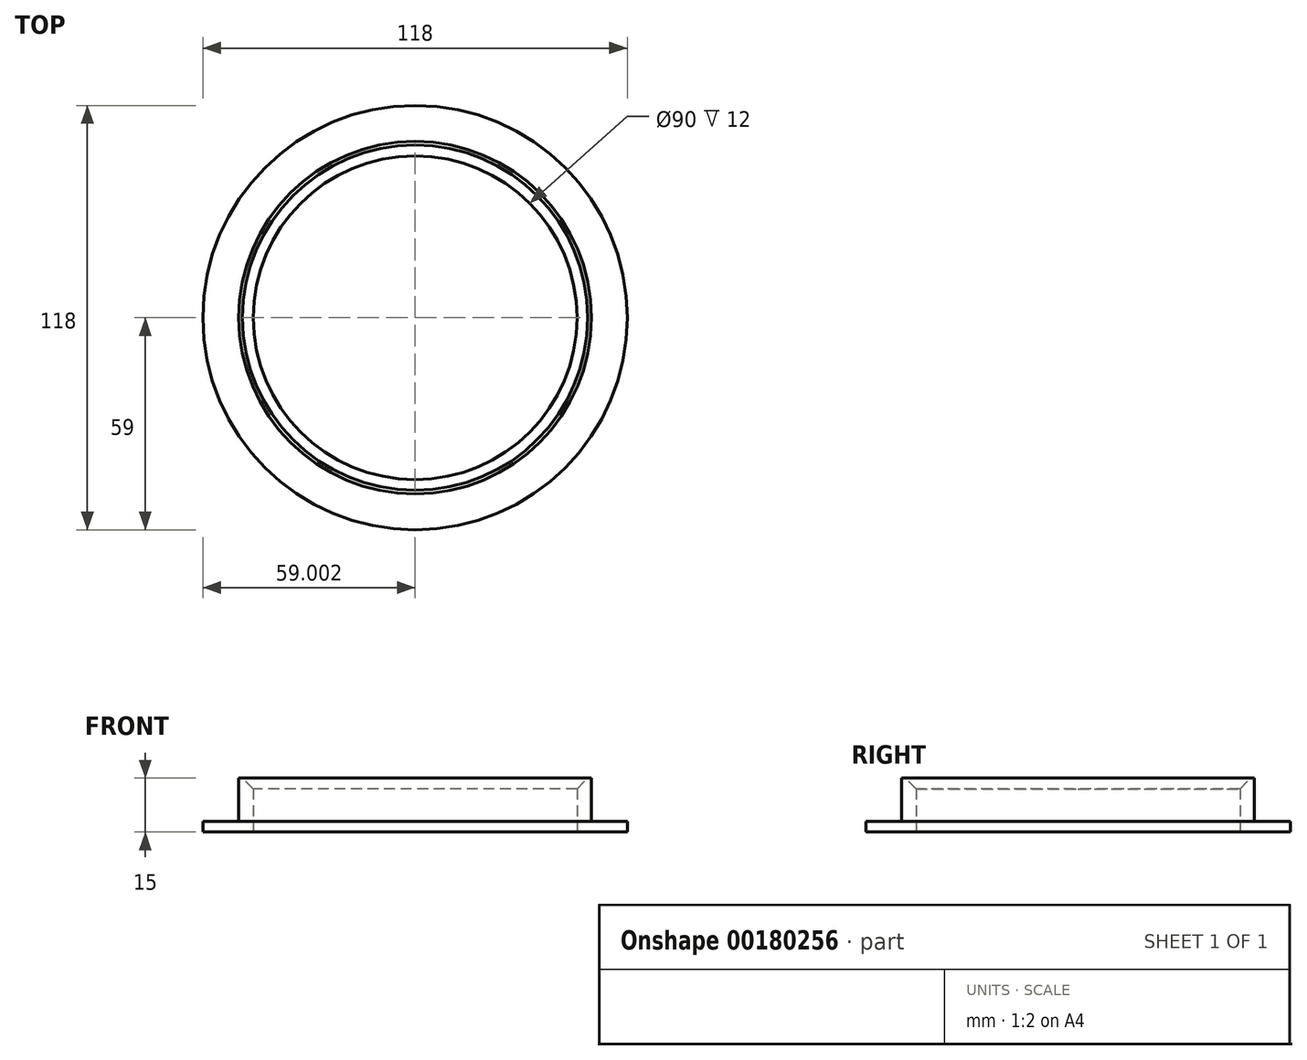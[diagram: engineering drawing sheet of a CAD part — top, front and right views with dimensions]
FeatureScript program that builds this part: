
annotation { "Feature Type Name" : "Feature", "Feature Type Description" : "" }
export const myFeature = defineFeature(function(context is Context, id is Id, definition is map)
    precondition{}
    {
        {
            var Q0;
            Q0=qCreatedBy(makeId("Top.planeOp"),FACE);
            var sketch = newSketch(context, id + "F0", { "sketchPlane" : qUnion([Q0])});
            skCircle(sketch, "E0", {"center": v(-35.22, 30.47) * mm, "radius": 45 * mm});
            skCircle(sketch, "E1.0", {"center": v(-35.22, 30.47) * mm, "radius": 49 * mm});
            skCircle(sketch, "E2.0", {"center": v(-35.22, 30.47) * mm, "radius": 59 * mm});
            skSolve(sketch);
        }
        {
            var Q0;
            Q0=makeQuery(id+"F0.imprint","IMPRINT",FACE,{"disambiguationData":[TD([[makeQuery(id+"F0.imprint","IMPRINT",EDGE,{"derivedFrom":sQuery(id+"F0.wireOp",EDGE,"E1.0")}),-1.0]])]});
            extrude(context, id + "F1", {"entities" : qUnion([Q0]), "depth" : 3 * mm});
        }
        {
            var Q0;
            Q0=makeQuery(id+"F0.imprint","IMPRINT",FACE,{"disambiguationData":[TD([[makeQuery(id+"F0.imprint","IMPRINT",EDGE,{"derivedFrom":sQuery(id+"F0.wireOp",EDGE,"E0")}),-1.0]])]});
            extrude(context, id + "F2", {"entities" : qUnion([Q0]), "operationType" : NewBodyOperationType.ADD, "depth" : 15 * mm});
        }
        {
            var Q0;
            Q0=makeQuery(id+"F2.opExtrude","CAP_EDGE",EDGE,{"disambiguationData":[OSD([sQuery(id+"F0.wireOp",EDGE,"E0")])],"isStart":false});
            chamfer(context, id + "F3", {"entities" : qUnion([Q0]), "width" : 3 * mm, "tangentPropagation" : true});
        }
    });
